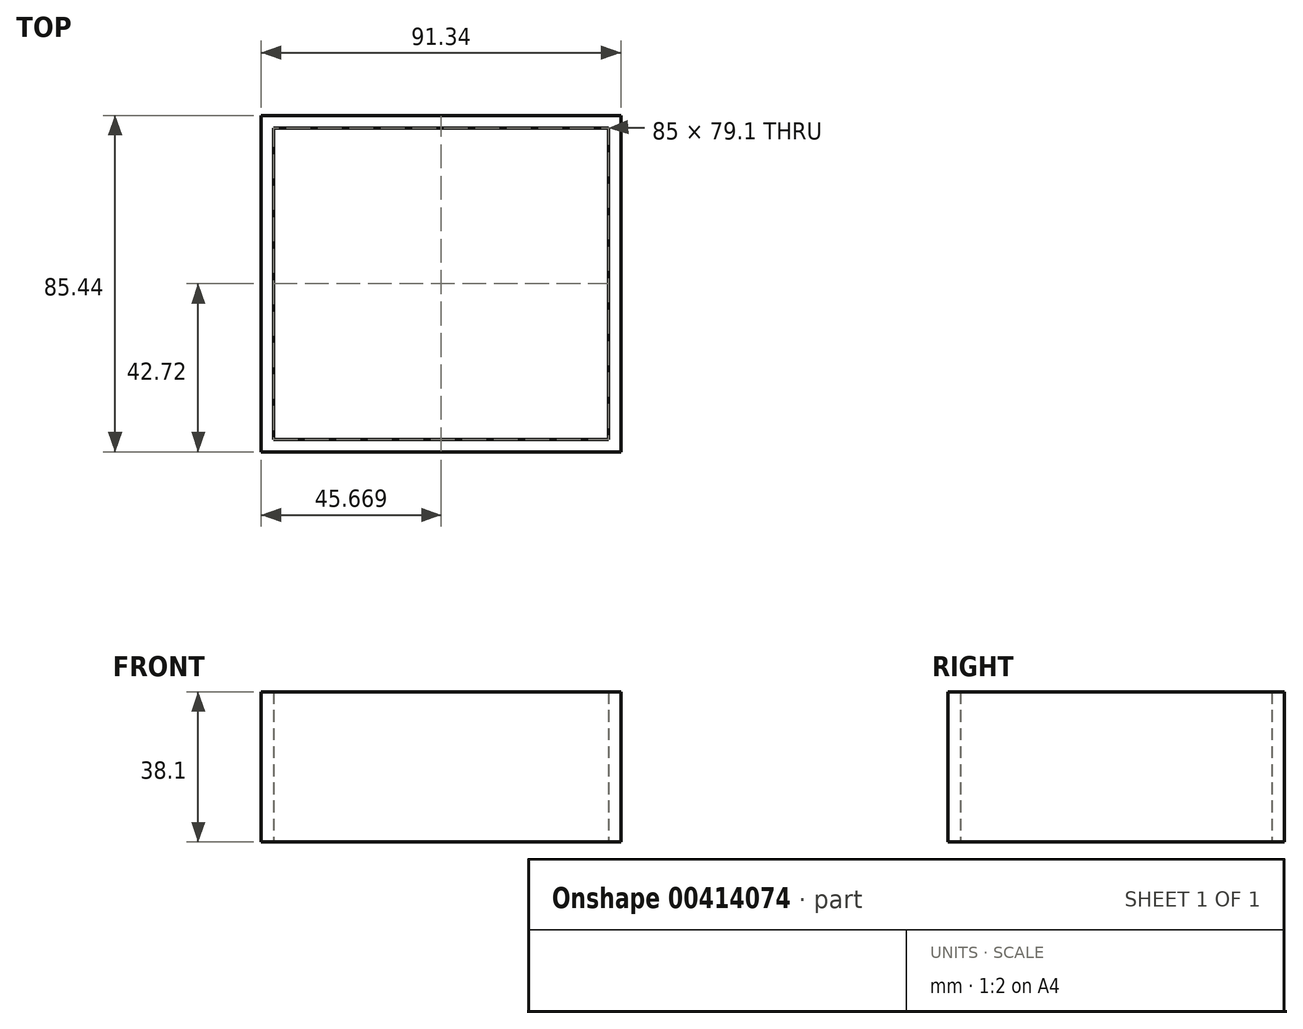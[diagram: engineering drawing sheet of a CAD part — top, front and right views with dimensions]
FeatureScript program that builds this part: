
annotation { "Feature Type Name" : "Feature", "Feature Type Description" : "" }
export const myFeature = defineFeature(function(context is Context, id is Id, definition is map)
    precondition{}
    {
        {
            var Q0;
            Q0=qCreatedBy(makeId("Top.planeOp"),FACE);
            var sketch = newSketch(context, id + "F0", { "sketchPlane" : qUnion([Q0])});
            skLineSegment(sketch, "E0.bottom", {"start": v(0, 0) * mm, "end": v(85, 0) * mm});
            skLineSegment(sketch, "E0.top", {"start": v(0, 79.1) * mm, "end": v(85, 79.1) * mm});
            skLineSegment(sketch, "E0.left", {"start": v(0, 0) * mm, "end": v(0, 79.1) * mm});
            skLineSegment(sketch, "E0.right", {"start": v(85, 0) * mm, "end": v(85, 79.1) * mm});
            skPoint(sketch, "E1", {"position": v(42.5, 39.55) * mm});
            skPoint(sketch, "E2.orphan", {"position": v(42.5, 79.1) * mm});
            skPoint(sketch, "E3.end.orphan", {"position": v(0, 39.55) * mm});
            skPoint(sketch, "E4.end.orphan", {"position": v(42.5, 0) * mm});
            skPoint(sketch, "E5.end.orphan", {"position": v(85, 39.55) * mm});
            skLineSegment(sketch, "E6.top", {"start": v(88.17, -3.18) * mm, "end": v(-3.17, -3.18) * mm});
            skLineSegment(sketch, "E6.right", {"start": v(-3.17, 82.27) * mm, "end": v(-3.17, -3.17) * mm});
            skPoint(sketch, "E6.left.start.orphan", {"position": v(88.17, 82.27) * mm});
            skLineSegment(sketch, "E7", {"start": v(-3.17, 82.27) * mm, "end": v(88.17, 82.27) * mm});
            skLineSegment(sketch, "E8", {"start": v(88.17, -3.18) * mm, "end": v(88.17, 82.27) * mm});
            skSolve(sketch);
        }
        {
            var Q0;
            Q0=makeQuery(id+"F0.imprint","IMPRINT",FACE,{"disambiguationData":[TD([[makeQuery(id+"F0.imprint","IMPRINT",EDGE,{"derivedFrom":sQuery(id+"F0.wireOp",EDGE,"E0.bottom")}),-1.0]])]});
            extrude(context, id + "F1", {"entities" : qUnion([Q0]), "depth" : 38.1 * mm});
        }
    });
